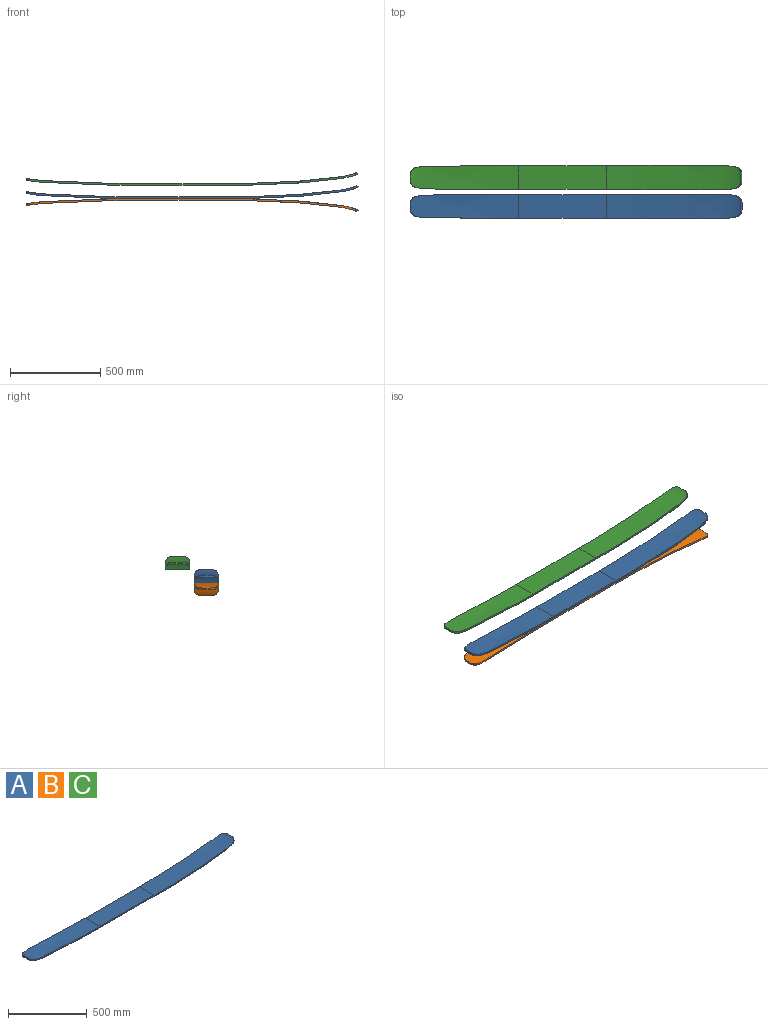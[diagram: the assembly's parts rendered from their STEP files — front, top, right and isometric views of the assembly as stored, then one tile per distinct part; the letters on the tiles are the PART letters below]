
ASSEMBLY  parts=3 mates=1
PART A: 26 faces, bbox 1840x136x73.2 mm
  f0: bspline ~67.73x17.51mm, area 676mm2, adj f1,f19,f20,f23
  f1: bspline ~38.9x32.19mm, area 534.7mm2, adj f0,f2,f20,f23
  f2: plane 31.63x9.66mm, normal (-0.97,0,0.26), area 316.3mm2, adj f1,f3,f20,f23
  f3: bspline ~38.9x32.19mm, area 534.7mm2, adj f2,f4,f20,f23
  f4: bspline ~67.73x17.51mm, area 676mm2, adj f3,f5,f20,f23
  f5: bspline ~384.09x25.61mm, area 3840mm2, adj f4,f6,f20,f23
  f6: bspline ~118.51x10.73mm, area 1184.5mm2, adj f5,f7,f20,f23
  f7: cylinder r=53603.82mm len=490mm, axis (0,0,1), area 4900mm2, adj f6,f8,f21,f24
  f8: bspline ~162.16x11.75mm, area 1620.6mm2, adj f7,f9,f22,f25
  f9: bspline ~493.15x45.77mm, area 4938.8mm2, adj f8,f10,f22,f25
  f10: bspline ~65.44x23.7mm, area 652.5mm2, adj f9,f11,f22,f25
  f11: bspline ~39.01x34.04mm, area 547.4mm2, adj f10,f12,f22,f25
  f12: plane 38.91x8.19mm, normal (0.82,0,0.57), area 389.1mm2, adj f11,f13,f22,f25
  f13: bspline ~39.01x34.04mm, area 547.4mm2, adj f12,f14,f22,f25
  f14: bspline ~65.44x23.7mm, area 652.5mm2, adj f13,f15,f22,f25
  f15: bspline ~493.15x45.77mm, area 4938.8mm2, adj f14,f16,f22,f25
  f16: bspline ~162.16x11.75mm, area 1620.6mm2, adj f15,f17,f22,f25
  f17: cylinder r=53603.82mm len=490mm, axis (0,0,1), area 4900mm2, adj f16,f18,f21,f24
  f18: bspline ~118.51x10.73mm, area 1184.5mm2, adj f17,f19,f20,f23
  f19: bspline ~384.09x25.61mm, area 3840mm2, adj f0,f18,f20,f23
  f20: extruded ~597.41x132mm, area 75667.6mm2, adj f0,f1,f2,f3,f4,f5,f6,f18
  f21: plane 490x131.9mm, normal (0,0,1), area 63933.3mm2, adj f7,f17,f20,f22
  f22: extruded ~744.26x136mm, area 98666.2mm2, adj f8,f9,f10,f11,f12,f13,f14,f15
  f23: extruded ~600x132mm, area 75890.8mm2, adj f0,f1,f2,f3,f4,f5,f6,f18
  f24: plane 490x131.9mm, normal (0,0,-1), area 63933.3mm2, adj f7,f17,f23,f25
  f25: extruded ~750x136mm, area 99229.3mm2, adj f8,f9,f10,f11,f12,f13,f14,f15
PART B: same geometry as A
PART C: same geometry as A
PLACE A t=(-195.65,-385.39,164.84)mm
PLACE B rot(axis=(1,0,0),180deg) t=(-195.65,-385.39,-15.16)mm
PLACE C t=(-196.02,-225.86,238.45)mm
MATE fastened B.f24 <-> A.f24  axis (0,0,1) through (-790.23,-385.39,74.84)mm
